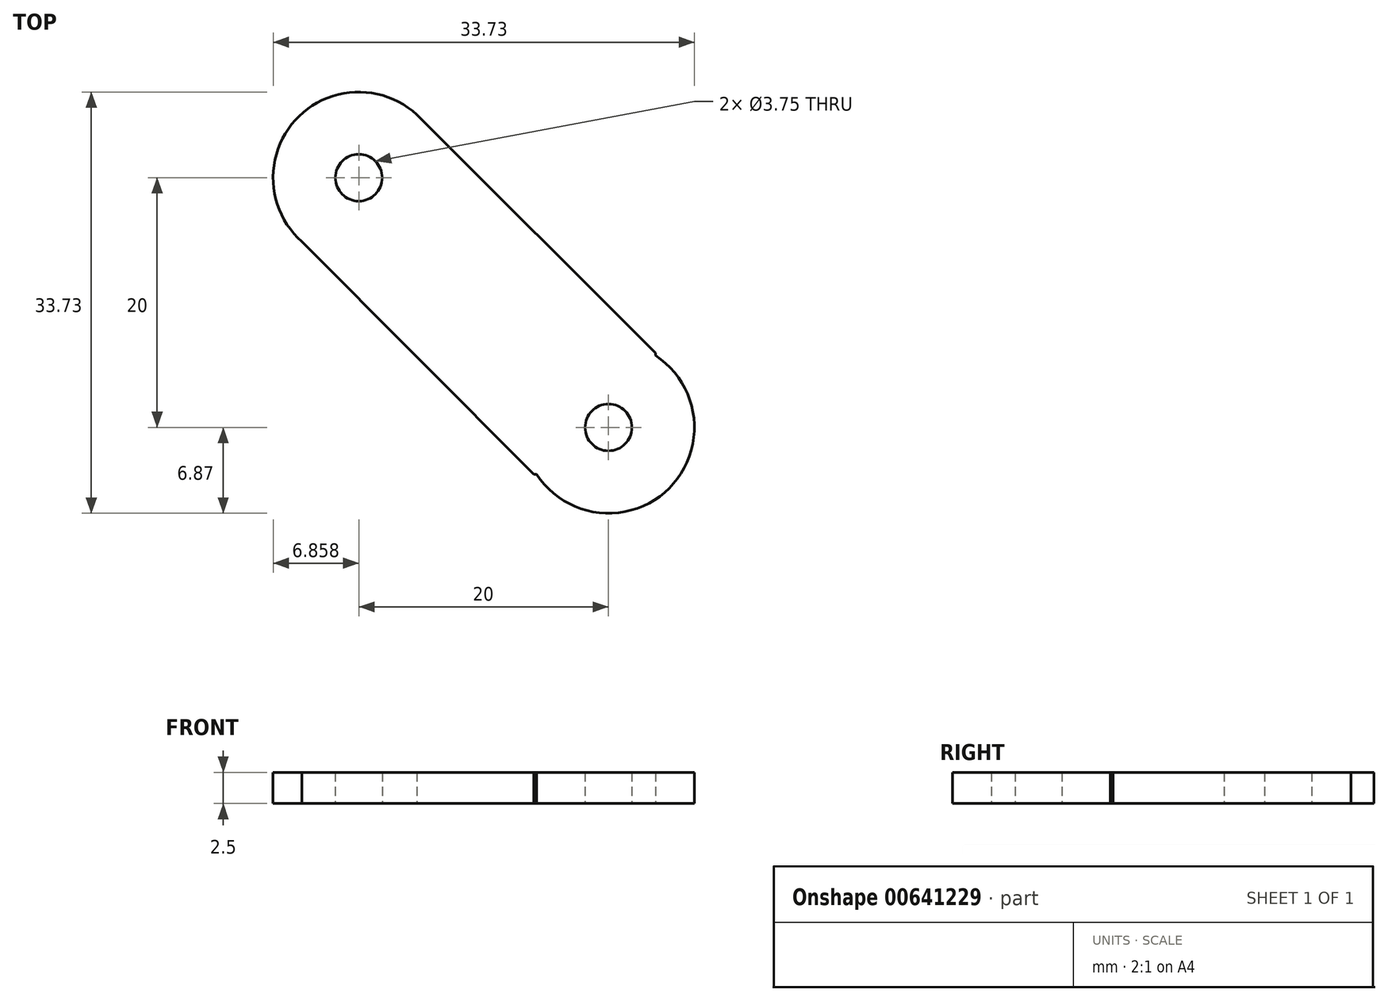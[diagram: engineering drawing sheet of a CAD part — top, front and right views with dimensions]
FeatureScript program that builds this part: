
annotation { "Feature Type Name" : "Feature", "Feature Type Description" : "" }
export const myFeature = defineFeature(function(context is Context, id is Id, definition is map)
    precondition{}
    {
        {
            var Q0;
            Q0=qCreatedBy(makeId("Top.planeOp"),FACE);
            var sketch = newSketch(context, id + "F0", { "sketchPlane" : qUnion([Q0])});
            skLineSegment(sketch, "E0.bottom", {"start": v(-70.68, -70) * mm, "end": v(-0.68, -70) * mm});
            skLineSegment(sketch, "E0.top", {"start": v(-70.68, 0) * mm, "end": v(-0.68, 0) * mm});
            skLineSegment(sketch, "E0.left", {"start": v(-70.68, -70) * mm, "end": v(-70.68, 0) * mm});
            skLineSegment(sketch, "E0.right", {"start": v(-0.68, -70) * mm, "end": v(-0.68, 0) * mm});
            skLineSegment(sketch, "E1.0", {"start": v(-90.68, -90) * mm, "end": v(-90.68, 20) * mm});
            skLineSegment(sketch, "E1.1", {"start": v(-90.68, -90) * mm, "end": v(19.32, -90) * mm});
            skLineSegment(sketch, "E1.2", {"start": v(19.32, -90) * mm, "end": v(19.32, 20) * mm});
            skLineSegment(sketch, "E1.3", {"start": v(-90.68, 20) * mm, "end": v(19.32, 20) * mm});
            skLineSegment(sketch, "E2.0", {"start": v(15.57, -86.25) * mm, "end": v(15.57, 20) * mm});
            skLineSegment(sketch, "E2.1", {"start": v(-51.83, -86.25) * mm, "end": v(15.57, -86.25) * mm});
            skCircle(sketch, "E3", {"center": v(15.57, -86.25) * mm, "radius": 1.88 * mm});
            skLineSegment(sketch, "E4.0", {"start": v(-4.43, -66.25) * mm, "end": v(-4.43, 0) * mm});
            skLineSegment(sketch, "E4.1", {"start": v(-31.83, -66.25) * mm, "end": v(-4.43, -66.25) * mm});
            skCircle(sketch, "E5", {"center": v(-4.43, -66.25) * mm, "radius": 1.88 * mm});
            skLineSegment(sketch, "E6", {"start": v(-5.96, -67.33) * mm, "end": v(14.24, -87.57) * mm});
            skLineSegment(sketch, "E7", {"start": v(-3.32, -64.74) * mm, "end": v(16.9, -84.92) * mm});
            skLineSegment(sketch, "E8.0", {"start": v(0.22, -61.2) * mm, "end": v(20.43, -81.39) * mm});
            skLineSegment(sketch, "E9.0", {"start": v(-9.5, -70.87) * mm, "end": v(10.7, -91.1) * mm});
            skCircle(sketch, "E10", {"center": v(-4.43, -66.25) * mm, "radius": 6.86 * mm});
            skCircle(sketch, "E11", {"center": v(15.57, -86.25) * mm, "radius": 6.88 * mm});
            skSolve(sketch);
        }
        {
            var Q0;
            {var subQ0=sQuery(id+"F0.wireOp",EDGE,"E5");var subQ1=sQuery(id+"F0.wireOp",EDGE,"E4.0");var subQ2=makeQuery(id+"F0.imprint","INTERSECT",VERTEX,{"derivedFrom":[subQ1,subQ0]});Q0=makeQuery(id+"F0.imprint","IMPRINT",FACE,{"disambiguationData":[TD([[makeQuery(id+"F0.imprint","IMPRINT",EDGE,{"disambiguationData":[TD([[subQ2,-1.0]])],"derivedFrom":subQ1}),1.0]])]});}
            var Q1;
            {var subQ6=sQuery(id+"F0.wireOp",EDGE,"E10");var subQ8=sQuery(id+"F0.wireOp",EDGE,"E0.bottom");var subQ9=makeQuery(id+"F0.imprint","INTERSECT",VERTEX,{"derivedFrom":[subQ8,subQ6]});Q1=makeQuery(id+"F0.imprint","IMPRINT",FACE,{"disambiguationData":[TD([[makeQuery(id+"F0.imprint","IMPRINT",EDGE,{"disambiguationData":[TD([[subQ9,-1.0]])],"derivedFrom":subQ8}),1.0]])]});}
            var Q2;
            {var subQ0=sQuery(id+"F0.wireOp",EDGE,"E10");var subQ1=sQuery(id+"F0.wireOp",EDGE,"E0.bottom");var subQ2=makeQuery(id+"F0.imprint","INTERSECT",VERTEX,{"derivedFrom":[subQ1,subQ0]});Q2=makeQuery(id+"F0.imprint","IMPRINT",FACE,{"disambiguationData":[TD([[makeQuery(id+"F0.imprint","IMPRINT",EDGE,{"disambiguationData":[TD([[subQ2,-1.0]])],"derivedFrom":subQ1}),-1.0]])]});}
            var Q3;
            {var subQ1=sQuery(id+"F0.wireOp",EDGE,"E0.bottom");var subQ7=sQuery(id+"F0.wireOp",EDGE,"E0.right");var subQ8=makeQuery(id+"F0.imprint","INTERSECT",VERTEX,{"derivedFrom":[subQ1,subQ7]});Q3=makeQuery(id+"F0.imprint","IMPRINT",FACE,{"disambiguationData":[TD([[makeQuery(id+"F0.imprint","IMPRINT",EDGE,{"disambiguationData":[TD([[subQ8,1.0]])],"derivedFrom":subQ1}),1.0]])]});}
            var Q4;
            {var subQ0=sQuery(id+"F0.wireOp",EDGE,"E7");var subQ8=sQuery(id+"F0.wireOp",EDGE,"E0.right");var subQ9=makeQuery(id+"F0.imprint","INTERSECT",VERTEX,{"derivedFrom":[subQ8,subQ0]});Q4=makeQuery(id+"F0.imprint","IMPRINT",FACE,{"disambiguationData":[TD([[makeQuery(id+"F0.imprint","IMPRINT",EDGE,{"disambiguationData":[TD([[subQ9,-1.0]])],"derivedFrom":subQ8}),1.0]])]});}
            var Q5;
            {var subQ4=sQuery(id+"F0.wireOp",EDGE,"E7");var subQ5=sQuery(id+"F0.wireOp",EDGE,"E0.right");var subQ6=makeQuery(id+"F0.imprint","INTERSECT",VERTEX,{"derivedFrom":[subQ5,subQ4]});Q5=makeQuery(id+"F0.imprint","IMPRINT",FACE,{"disambiguationData":[TD([[makeQuery(id+"F0.imprint","IMPRINT",EDGE,{"disambiguationData":[TD([[subQ6,-1.0]])],"derivedFrom":subQ5}),-1.0]])]});}
            var Q6;
            {var subQ1=sQuery(id+"F0.wireOp",EDGE,"E0.right");var subQ5=sQuery(id+"F0.wireOp",EDGE,"E0.bottom");var subQ6=makeQuery(id+"F0.imprint","INTERSECT",VERTEX,{"derivedFrom":[subQ5,subQ1]});Q6=makeQuery(id+"F0.imprint","IMPRINT",FACE,{"disambiguationData":[TD([[makeQuery(id+"F0.imprint","IMPRINT",EDGE,{"disambiguationData":[TD([[subQ6,1.0]])],"derivedFrom":subQ5}),-1.0]])]});}
            var Q7;
            {var subQ1=sQuery(id+"F0.wireOp",EDGE,"E9.0");var subQ7=sQuery(id+"F0.wireOp",EDGE,"E2.1");var subQ8=makeQuery(id+"F0.imprint","INTERSECT",VERTEX,{"derivedFrom":[subQ7,subQ1]});Q7=makeQuery(id+"F0.imprint","IMPRINT",FACE,{"disambiguationData":[TD([[makeQuery(id+"F0.imprint","IMPRINT",EDGE,{"disambiguationData":[TD([[subQ8,-1.0]])],"derivedFrom":subQ7}),1.0]])]});}
            var Q8;
            {var subQ0=sQuery(id+"F0.wireOp",EDGE,"E10");var subQ1=sQuery(id+"F0.wireOp",EDGE,"E6");var subQ2=makeQuery(id+"F0.imprint","INTERSECT",VERTEX,{"derivedFrom":[subQ1,subQ0]});Q8=makeQuery(id+"F0.imprint","IMPRINT",FACE,{"disambiguationData":[TD([[makeQuery(id+"F0.imprint","IMPRINT",EDGE,{"disambiguationData":[TD([[subQ2,-1.0]])],"derivedFrom":subQ1}),1.0]])]});}
            var Q9;
            {var subQ5=sQuery(id+"F0.wireOp",EDGE,"E2.0");var subQ7=sQuery(id+"F0.wireOp",EDGE,"E11");var subQ9=makeQuery(id+"F0.imprint","INTERSECT",VERTEX,{"derivedFrom":[subQ5,subQ7]});Q9=makeQuery(id+"F0.imprint","IMPRINT",FACE,{"disambiguationData":[TD([[makeQuery(id+"F0.imprint","IMPRINT",EDGE,{"disambiguationData":[TD([[subQ9,-1.0]])],"derivedFrom":subQ5}),1.0]])]});}
            var Q10;
            {var subQ0=sQuery(id+"F0.wireOp",EDGE,"E7");var subQ1=sQuery(id+"F0.wireOp",EDGE,"E2.0");var subQ2=makeQuery(id+"F0.imprint","INTERSECT",VERTEX,{"derivedFrom":[subQ1,subQ0]});Q10=makeQuery(id+"F0.imprint","IMPRINT",FACE,{"disambiguationData":[TD([[makeQuery(id+"F0.imprint","IMPRINT",EDGE,{"disambiguationData":[TD([[subQ2,-1.0]])],"derivedFrom":subQ1}),1.0]])]});}
            var Q11;
            {var subQ5=sQuery(id+"F0.wireOp",EDGE,"E3");var subQ6=sQuery(id+"F0.wireOp",EDGE,"E2.0");var subQ7=makeQuery(id+"F0.imprint","INTERSECT",VERTEX,{"derivedFrom":[subQ6,subQ5]});Q11=makeQuery(id+"F0.imprint","IMPRINT",FACE,{"disambiguationData":[TD([[makeQuery(id+"F0.imprint","IMPRINT",EDGE,{"disambiguationData":[TD([[subQ7,-1.0]])],"derivedFrom":subQ6}),1.0]])]});}
            var Q12;
            {var subQ0=sQuery(id+"F0.wireOp",EDGE,"E11");var subQ1=sQuery(id+"F0.wireOp",EDGE,"E2.1");var subQ2=makeQuery(id+"F0.imprint","INTERSECT",VERTEX,{"derivedFrom":[subQ1,subQ0]});Q12=makeQuery(id+"F0.imprint","IMPRINT",FACE,{"disambiguationData":[TD([[makeQuery(id+"F0.imprint","IMPRINT",EDGE,{"disambiguationData":[TD([[subQ2,-1.0]])],"derivedFrom":subQ1}),1.0]])]});}
            var Q13;
            {var subQ0=sQuery(id+"F0.wireOp",EDGE,"E9.0");var subQ1=sQuery(id+"F0.wireOp",EDGE,"E1.1");var subQ2=makeQuery(id+"F0.imprint","INTERSECT",VERTEX,{"derivedFrom":[subQ1,subQ0]});Q13=makeQuery(id+"F0.imprint","IMPRINT",FACE,{"disambiguationData":[TD([[makeQuery(id+"F0.imprint","IMPRINT",EDGE,{"disambiguationData":[TD([[subQ2,-1.0]])],"derivedFrom":subQ1}),1.0]])]});}
            var Q14;
            {var subQ0=sQuery(id+"F0.wireOp",EDGE,"E8.0");var subQ1=sQuery(id+"F0.wireOp",EDGE,"E1.2");var subQ2=makeQuery(id+"F0.imprint","INTERSECT",VERTEX,{"derivedFrom":[subQ1,subQ0]});Q14=makeQuery(id+"F0.imprint","IMPRINT",FACE,{"disambiguationData":[TD([[makeQuery(id+"F0.imprint","IMPRINT",EDGE,{"disambiguationData":[TD([[subQ2,1.0]])],"derivedFrom":subQ1}),1.0]])]});}
            var Q15;
            {var subQ0=sQuery(id+"F0.wireOp",EDGE,"E6");var subQ1=sQuery(id+"F0.wireOp",EDGE,"E2.1");var subQ2=makeQuery(id+"F0.imprint","INTERSECT",VERTEX,{"derivedFrom":[subQ1,subQ0]});Q15=makeQuery(id+"F0.imprint","IMPRINT",FACE,{"disambiguationData":[TD([[makeQuery(id+"F0.imprint","IMPRINT",EDGE,{"disambiguationData":[TD([[subQ2,-1.0]])],"derivedFrom":subQ1}),-1.0]])]});}
            var Q16;
            {var subQ0=sQuery(id+"F0.wireOp",EDGE,"E3");var subQ1=sQuery(id+"F0.wireOp",EDGE,"E2.0");var subQ2=makeQuery(id+"F0.imprint","INTERSECT",VERTEX,{"derivedFrom":[subQ1,subQ0]});Q16=makeQuery(id+"F0.imprint","IMPRINT",FACE,{"disambiguationData":[TD([[makeQuery(id+"F0.imprint","IMPRINT",EDGE,{"disambiguationData":[TD([[subQ2,-1.0]])],"derivedFrom":subQ1}),-1.0]])]});}
            var Q17;
            {var subQ5=sQuery(id+"F0.wireOp",EDGE,"E1.2");var subQ6=sQuery(id+"F0.wireOp",EDGE,"E1.1");var subQ7=makeQuery(id+"F0.imprint","INTERSECT",VERTEX,{"derivedFrom":[subQ6,subQ5]});Q17=makeQuery(id+"F0.imprint","IMPRINT",FACE,{"disambiguationData":[TD([[makeQuery(id+"F0.imprint","IMPRINT",EDGE,{"disambiguationData":[TD([[subQ7,1.0]])],"derivedFrom":subQ6}),1.0]])]});}
            var Q18;
            {var subQ2=sQuery(id+"F0.wireOp",EDGE,"E1.1");var subQ5=sQuery(id+"F0.wireOp",EDGE,"E1.2");var subQ7=makeQuery(id+"F0.imprint","INTERSECT",VERTEX,{"derivedFrom":[subQ2,subQ5]});Q18=makeQuery(id+"F0.imprint","IMPRINT",FACE,{"disambiguationData":[TD([[makeQuery(id+"F0.imprint","IMPRINT",EDGE,{"disambiguationData":[TD([[subQ7,1.0]])],"derivedFrom":subQ2}),-1.0]])]});}
            extrude(context, id + "F1", {"entities" : qUnion([Q0, Q1, Q2, Q3, Q4, Q5, Q6, Q7, Q8, Q9, Q10, Q11, Q12, Q13, Q14, Q15, Q16, Q17, Q18]), "depth" : 2.5 * mm, "offsetDistance" : 25 * mm});
        }
    });
